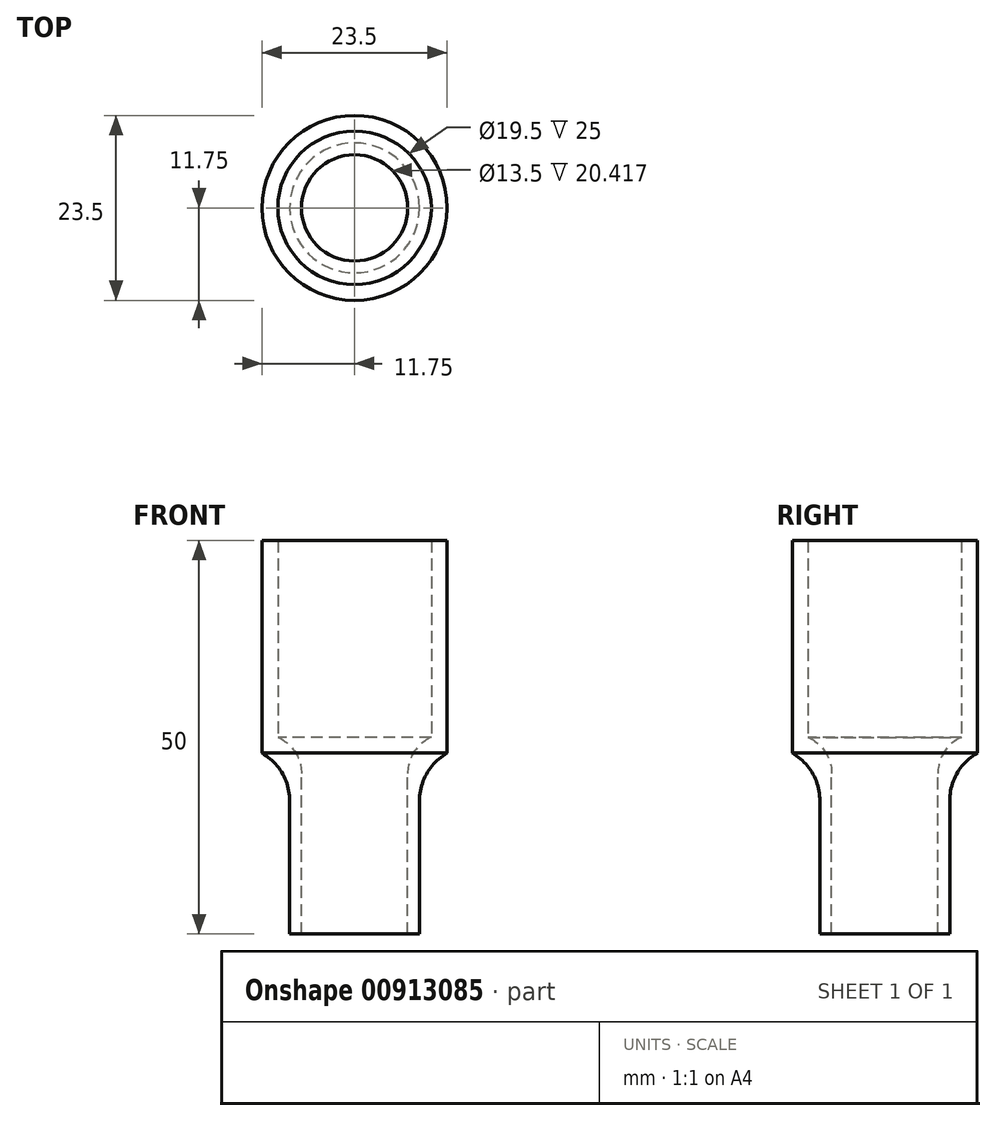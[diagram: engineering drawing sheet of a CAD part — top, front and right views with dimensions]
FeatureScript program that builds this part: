
annotation { "Feature Type Name" : "Feature", "Feature Type Description" : "" }
export const myFeature = defineFeature(function(context is Context, id is Id, definition is map)
    precondition{}
    {
        {
            var Q0;
            Q0=qCreatedBy(makeId("Top.planeOp"),FACE);
            var sketch = newSketch(context, id + "F0", { "sketchPlane" : qUnion([Q0])});
            skCircle(sketch, "E0", {"center": v(0, 0) * mm, "radius": 9.75 * mm});
            skCircle(sketch, "E1", {"center": v(0, 0) * mm, "radius": 11.75 * mm});
            skCircle(sketch, "E2", {"center": v(0, 0) * mm, "radius": 8.25 * mm});
            skCircle(sketch, "E3", {"center": v(0, 0) * mm, "radius": 6.75 * mm});
            skSolve(sketch);
        }
        {
            var Q0;
            Q0=qSketchRegion(id+"F0",true);
            extrude(context, id + "F1", {"entities" : qUnion([Q0]), "depth" : 25 * mm, "offsetDistance" : 25 * mm});
        }
        {
            var Q0;
            Q0=makeQuery(id+"F0.imprint","IMPRINT",FACE,{"disambiguationData":[TD([[makeQuery(id+"F0.imprint","IMPRINT",EDGE,{"derivedFrom":sQuery(id+"F0.wireOp",EDGE,"E0")}),1.0]])]});
            var Q1;
            Q1=makeQuery(id+"F0.imprint","IMPRINT",FACE,{"disambiguationData":[TD([[makeQuery(id+"F0.imprint","IMPRINT",EDGE,{"derivedFrom":sQuery(id+"F0.wireOp",EDGE,"E0")}),-1.0]])]});
            var Q2;
            Q2=makeQuery(id+"F0.imprint","IMPRINT",FACE,{"disambiguationData":[TD([[makeQuery(id+"F0.imprint","IMPRINT",EDGE,{"derivedFrom":sQuery(id+"F0.wireOp",EDGE,"E2")}),1.0]])]});
            extrude(context, id + "F2", {"entities" : qUnion([Q0, Q1, Q2]), "operationType" : NewBodyOperationType.ADD, "oppositeDirection" : true, "depth" : 2 * mm, "offsetDistance" : 25 * mm});
        }
        {
            var Q0;
            Q0=makeQuery(id+"F0.imprint","IMPRINT",FACE,{"disambiguationData":[TD([[makeQuery(id+"F0.imprint","IMPRINT",EDGE,{"derivedFrom":sQuery(id+"F0.wireOp",EDGE,"E2")}),1.0]])]});
            extrude(context, id + "F3", {"entities" : qUnion([Q0]), "operationType" : NewBodyOperationType.ADD, "oppositeDirection" : true, "depth" : 25 * mm, "offsetDistance" : 25 * mm});
        }
        {
            var Q0;
            Q0=makeQuery(id+"F3.boolean.opBoolean","INTERSECT",EDGE,{"derivedFrom":[makeQuery(id+"F2.opExtrude","CAP_FACE",FACE,{"disambiguationData":[OSD([sQuery(id+"F0.wireOp",EDGE,"E1"),sQuery(id+"F0.wireOp",EDGE,"E3")])],"isStart":false}),makeQuery(id+"F3.opExtrude","SWEPT_FACE",FACE,{"disambiguationData":[OSD([sQuery(id+"F0.wireOp",EDGE,"E2")])]})]});
            fillet(context, id + "F4", {"entities" : qUnion([Q0]), "radius" : 7 * mm, "tangentPropagation" : true, "allowEdgeOverflow" : false});
        }
        {
            var Q0;
            Q0=makeQuery(id+"F2.opExtrude","CAP_EDGE",EDGE,{"disambiguationData":[OSD([sQuery(id+"F0.wireOp",EDGE,"E3")])],"isStart":true});
            fillet(context, id + "F5", {"entities" : qUnion([Q0]), "radius" : 5 * mm, "tangentPropagation" : true, "allowEdgeOverflow" : false});
        }
    });
